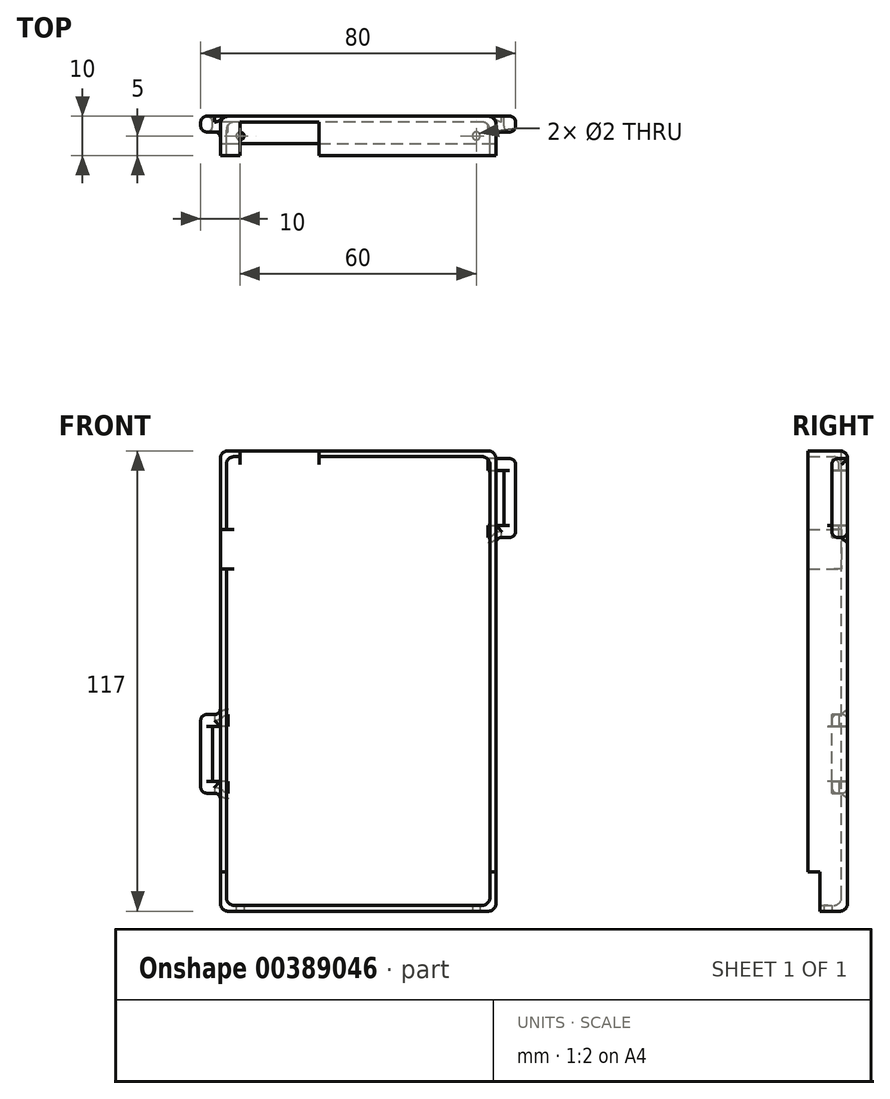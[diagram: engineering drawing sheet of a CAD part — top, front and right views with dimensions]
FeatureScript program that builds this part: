
annotation { "Feature Type Name" : "Feature", "Feature Type Description" : "" }
export const myFeature = defineFeature(function(context is Context, id is Id, definition is map)
    precondition{}
    {
        {
            var Q0;
            Q0=qCreatedBy(makeId("Front.planeOp"),FACE);
            var sketch = newSketch(context, id + "F0", { "sketchPlane" : qUnion([Q0])});
            skLineSegment(sketch, "E0.bottom", {"start": v(-70, 117) * mm, "end": v(0, 117) * mm});
            skLineSegment(sketch, "E0.top", {"start": v(-70, 0) * mm, "end": v(0, 0) * mm});
            skLineSegment(sketch, "E0.left", {"start": v(-70, 117) * mm, "end": v(-70, 0) * mm});
            skLineSegment(sketch, "E0.right", {"start": v(0, 117) * mm, "end": v(0, 0) * mm});
            skLineSegment(sketch, "E1.0", {"start": v(-68.5, 115.5) * mm, "end": v(-1.5, 115.5) * mm});
            skLineSegment(sketch, "E1.1", {"start": v(-68.5, 115.5) * mm, "end": v(-68.5, 1.5) * mm});
            skLineSegment(sketch, "E1.2", {"start": v(-68.5, 1.5) * mm, "end": v(-1.5, 1.5) * mm});
            skLineSegment(sketch, "E1.3", {"start": v(-1.5, 115.5) * mm, "end": v(-1.5, 1.5) * mm});
            skLineSegment(sketch, "E2.bottom", {"start": v(-70, 97) * mm, "end": v(-68.5, 97) * mm});
            skLineSegment(sketch, "E2.top", {"start": v(-70, 87) * mm, "end": v(-68.5, 87) * mm});
            skLineSegment(sketch, "E2.left", {"start": v(-70, 97) * mm, "end": v(-70, 87) * mm});
            skLineSegment(sketch, "E2.right", {"start": v(-68.5, 97) * mm, "end": v(-68.5, 87) * mm});
            skLineSegment(sketch, "E3.bottom", {"start": v(-65, 117) * mm, "end": v(-45, 117) * mm});
            skLineSegment(sketch, "E3.top", {"start": v(-65, 115.5) * mm, "end": v(-45, 115.5) * mm});
            skLineSegment(sketch, "E3.left", {"start": v(-65, 117) * mm, "end": v(-65, 115.5) * mm});
            skLineSegment(sketch, "E3.right", {"start": v(-45, 117) * mm, "end": v(-45, 115.5) * mm});
            skSolve(sketch);
        }
        {
            var Q0;
            Q0=qSketchRegion(id+"F0",true);
            var Q1;
            Q1=makeQuery(id+"F0.imprint","IMPRINT",FACE,{"disambiguationData":[TD([[makeQuery(id+"F0.imprint","IMPRINT",EDGE,{"derivedFrom":sQuery(id+"F0.wireOp",EDGE,"E0.bottom")}),-1.0]])]});
            var Q2;
            Q2=makeQuery(id+"F0.imprint","IMPRINT",FACE,{"disambiguationData":[TD([[makeQuery(id+"F0.imprint","IMPRINT",EDGE,{"derivedFrom":sQuery(id+"F0.wireOp",EDGE,"E1.0")}),-1.0]])]});
            extrude(context, id + "F1", {"entities" : qUnion([Q0, Q1, Q2]), "depth" : 1.5 * mm});
        }
        {
            var Q0;
            {var subQ4=sQuery(id+"F0.wireOp",EDGE,"E2.bottom");Q0=makeQuery(id+"F0.imprint","IMPRINT",FACE,{"disambiguationData":[TD([[makeQuery(id+"F0.imprint","IMPRINT",EDGE,{"derivedFrom":subQ4}),1.0]])]});}
            var Q1;
            {var subQ2=sQuery(id+"F0.wireOp",EDGE,"E0.top");Q1=makeQuery(id+"F0.imprint","IMPRINT",FACE,{"disambiguationData":[TD([[makeQuery(id+"F0.imprint","IMPRINT",EDGE,{"derivedFrom":subQ2}),1.0]])]});}
            extrude(context, id + "F2", {"entities" : qUnion([Q0, Q1]), "operationType" : NewBodyOperationType.ADD, "depth" : 10 * mm});
        }
        {
            var Q0;
            {var subQ0=sQuery(id+"F0.wireOp",EDGE,"E0.top");Q0=makeQuery(id+"F2.boolean.opBoolean","MERGE",FACE,{"derivedFrom":[makeQuery(id+"F1.opExtrude","SWEPT_FACE",FACE,{"disambiguationData":[OSD([subQ0])]}),makeQuery(id+"F2.opExtrude","SWEPT_FACE",FACE,{"disambiguationData":[OSD([subQ0])]})]});}
            var sketch = newSketch(context, id + "F3", { "sketchPlane" : qUnion([Q0])});
            skCircle(sketch, "E4", {"center": v(-65, 5) * mm, "radius": 1 * mm});
            skLineSegment(sketch, "E5.0", {"start": v(-70, 10) * mm, "end": v(0, 10) * mm});
            skLineSegment(sketch, "E6.0", {"start": v(-70, 10) * mm, "end": v(-70, 0) * mm});
            skCircle(sketch, "E7", {"center": v(-5, 5) * mm, "radius": 1 * mm});
            skSolve(sketch);
        }
        {
            var Q0;
            Q0=qSketchRegion(id+"F3",true);
            extrude(context, id + "F4", {"entities" : qUnion([Q0]), "operationType" : NewBodyOperationType.REMOVE, "oppositeDirection" : true, "depth" : 25 * mm});
        }
        {
            var Q0;
            Q0=makeQuery(id+"F1.opExtrude","CAP_EDGE",EDGE,{"disambiguationData":[OSD([sQuery(id+"F0.wireOp",EDGE,"E0.top")])],"isStart":true});
            var Q1;
            Q1=makeQuery(id+"F1.opExtrude","CAP_EDGE",EDGE,{"disambiguationData":[OSD([sQuery(id+"F0.wireOp",EDGE,"E0.right")])],"isStart":true});
            var Q2;
            Q2=makeQuery(id+"F1.opExtrude","CAP_EDGE",EDGE,{"disambiguationData":[OSD([sQuery(id+"F0.wireOp",EDGE,"E0.left"),sQuery(id+"F0.wireOp",EDGE,"E2.left")])],"isStart":true});
            var Q3;
            Q3=makeQuery(id+"F1.opExtrude","CAP_EDGE",EDGE,{"disambiguationData":[OSD([sQuery(id+"F0.wireOp",EDGE,"E0.bottom"),sQuery(id+"F0.wireOp",EDGE,"E3.bottom")])],"isStart":true});
            var Q4;
            Q4=makeQuery(id+"F2.boolean.opBoolean","INTERSECT",EDGE,{"derivedFrom":[makeQuery(id+"F1.opExtrude","CAP_FACE",FACE,{"disambiguationData":[OSD([sQuery(id+"F0.wireOp",EDGE,"E0.bottom"),sQuery(id+"F0.wireOp",EDGE,"E0.top"),sQuery(id+"F0.wireOp",EDGE,"E0.left"),sQuery(id+"F0.wireOp",EDGE,"E0.right"),sQuery(id+"F0.wireOp",EDGE,"E2.left"),sQuery(id+"F0.wireOp",EDGE,"E3.bottom")])],"isStart":false}),makeQuery(id+"F2.opExtrude","SWEPT_FACE",FACE,{"disambiguationData":[OSD([sQuery(id+"F0.wireOp",EDGE,"E1.2")])]})]});
            var Q5;
            {var subQ0=sQuery(id+"F0.wireOp",EDGE,"E1.1");Q5=makeQuery(id+"F2.boolean.opBoolean","INTERSECT",EDGE,{"derivedFrom":[makeQuery(id+"F1.opExtrude","CAP_FACE",FACE,{"disambiguationData":[OSD([sQuery(id+"F0.wireOp",EDGE,"E0.bottom"),sQuery(id+"F0.wireOp",EDGE,"E0.top"),sQuery(id+"F0.wireOp",EDGE,"E0.left"),sQuery(id+"F0.wireOp",EDGE,"E0.right"),sQuery(id+"F0.wireOp",EDGE,"E2.left"),sQuery(id+"F0.wireOp",EDGE,"E3.bottom")])],"isStart":false}),makeQuery(id+"F2.opExtrude","SWEPT_FACE",FACE,{"disambiguationData":[OSD([subQ0]),TDD([makeQuery(id+"F0.imprint","IMPRINT",EDGE,{"disambiguationData":[TD([[makeQuery(id+"F0.imprint","INTERSECT",VERTEX,{"derivedFrom":[subQ0,sQuery(id+"F0.wireOp",EDGE,"E1.2")]}),1.0]])],"derivedFrom":subQ0})])]})]});}
            var Q6;
            {var subQ0=sQuery(id+"F0.wireOp",EDGE,"E1.1");Q6=makeQuery(id+"F2.boolean.opBoolean","INTERSECT",EDGE,{"derivedFrom":[makeQuery(id+"F1.opExtrude","CAP_FACE",FACE,{"disambiguationData":[OSD([sQuery(id+"F0.wireOp",EDGE,"E0.bottom"),sQuery(id+"F0.wireOp",EDGE,"E0.top"),sQuery(id+"F0.wireOp",EDGE,"E0.left"),sQuery(id+"F0.wireOp",EDGE,"E0.right"),sQuery(id+"F0.wireOp",EDGE,"E2.left"),sQuery(id+"F0.wireOp",EDGE,"E3.bottom")])],"isStart":false}),makeQuery(id+"F2.opExtrude","SWEPT_FACE",FACE,{"disambiguationData":[OSD([subQ0]),TDD([makeQuery(id+"F0.imprint","IMPRINT",EDGE,{"disambiguationData":[TD([[makeQuery(id+"F0.imprint","INTERSECT",VERTEX,{"derivedFrom":[sQuery(id+"F0.wireOp",EDGE,"E1.0"),subQ0]}),-1.0]])],"derivedFrom":subQ0})])]})]});}
            var Q7;
            {var subQ0=sQuery(id+"F0.wireOp",EDGE,"E1.0");Q7=makeQuery(id+"F2.boolean.opBoolean","INTERSECT",EDGE,{"derivedFrom":[makeQuery(id+"F1.opExtrude","CAP_FACE",FACE,{"disambiguationData":[OSD([sQuery(id+"F0.wireOp",EDGE,"E0.bottom"),sQuery(id+"F0.wireOp",EDGE,"E0.top"),sQuery(id+"F0.wireOp",EDGE,"E0.left"),sQuery(id+"F0.wireOp",EDGE,"E0.right"),sQuery(id+"F0.wireOp",EDGE,"E2.left"),sQuery(id+"F0.wireOp",EDGE,"E3.bottom")])],"isStart":false}),makeQuery(id+"F2.opExtrude","SWEPT_FACE",FACE,{"disambiguationData":[OSD([subQ0]),TDD([makeQuery(id+"F0.imprint","IMPRINT",EDGE,{"disambiguationData":[TD([[makeQuery(id+"F0.imprint","INTERSECT",VERTEX,{"derivedFrom":[subQ0,sQuery(id+"F0.wireOp",EDGE,"E1.1")]}),-1.0]])],"derivedFrom":subQ0})])]})]});}
            var Q8;
            {var subQ0=sQuery(id+"F0.wireOp",EDGE,"E1.0");Q8=makeQuery(id+"F2.boolean.opBoolean","INTERSECT",EDGE,{"derivedFrom":[makeQuery(id+"F1.opExtrude","CAP_FACE",FACE,{"disambiguationData":[OSD([sQuery(id+"F0.wireOp",EDGE,"E0.bottom"),sQuery(id+"F0.wireOp",EDGE,"E0.top"),sQuery(id+"F0.wireOp",EDGE,"E0.left"),sQuery(id+"F0.wireOp",EDGE,"E0.right"),sQuery(id+"F0.wireOp",EDGE,"E2.left"),sQuery(id+"F0.wireOp",EDGE,"E3.bottom")])],"isStart":false}),makeQuery(id+"F2.opExtrude","SWEPT_FACE",FACE,{"disambiguationData":[OSD([subQ0]),TDD([makeQuery(id+"F0.imprint","IMPRINT",EDGE,{"disambiguationData":[TD([[makeQuery(id+"F0.imprint","INTERSECT",VERTEX,{"derivedFrom":[subQ0,sQuery(id+"F0.wireOp",EDGE,"E1.3")]}),1.0]])],"derivedFrom":subQ0})])]})]});}
            var Q9;
            Q9=makeQuery(id+"F2.boolean.opBoolean","INTERSECT",EDGE,{"derivedFrom":[makeQuery(id+"F1.opExtrude","CAP_FACE",FACE,{"disambiguationData":[OSD([sQuery(id+"F0.wireOp",EDGE,"E0.bottom"),sQuery(id+"F0.wireOp",EDGE,"E0.top"),sQuery(id+"F0.wireOp",EDGE,"E0.left"),sQuery(id+"F0.wireOp",EDGE,"E0.right"),sQuery(id+"F0.wireOp",EDGE,"E2.left"),sQuery(id+"F0.wireOp",EDGE,"E3.bottom")])],"isStart":false}),makeQuery(id+"F2.opExtrude","SWEPT_FACE",FACE,{"disambiguationData":[OSD([sQuery(id+"F0.wireOp",EDGE,"E1.3")])]})]});
            fillet(context, id + "F5", {"entities" : qUnion([Q0, Q1, Q2, Q3, Q4, Q5, Q6, Q7, Q8, Q9]), "radius" : 2 * mm, "tangentPropagation" : true, "allowEdgeOverflow" : false});
        }
        {
            var Q0;
            {var subQ0=sQuery(id+"F0.wireOp",EDGE,"E0.left");var subQ1=sQuery(id+"F0.wireOp",EDGE,"E0.top");Q0=makeQuery(id+"F2.boolean.opBoolean","MERGE",EDGE,{"derivedFrom":[makeQuery(id+"F1.opExtrude","SWEPT_EDGE",EDGE,{"disambiguationData":[OSD([subQ1,subQ0])]}),makeQuery(id+"F2.opExtrude","SWEPT_EDGE",EDGE,{"disambiguationData":[OSD([subQ1,subQ0])]})]});}
            var Q1;
            {var subQ0=sQuery(id+"F0.wireOp",EDGE,"E0.right");var subQ1=sQuery(id+"F0.wireOp",EDGE,"E0.top");Q1=makeQuery(id+"F2.boolean.opBoolean","MERGE",EDGE,{"derivedFrom":[makeQuery(id+"F1.opExtrude","SWEPT_EDGE",EDGE,{"disambiguationData":[OSD([subQ1,subQ0])]}),makeQuery(id+"F2.opExtrude","SWEPT_EDGE",EDGE,{"disambiguationData":[OSD([subQ1,subQ0])]})]});}
            var Q2;
            Q2=makeQuery(id+"F2.opExtrude","SWEPT_EDGE",EDGE,{"disambiguationData":[OSD([sQuery(id+"F0.wireOp",EDGE,"E1.1"),sQuery(id+"F0.wireOp",EDGE,"E1.2")])]});
            var Q3;
            Q3=makeQuery(id+"F2.opExtrude","SWEPT_EDGE",EDGE,{"disambiguationData":[OSD([sQuery(id+"F0.wireOp",EDGE,"E1.2"),sQuery(id+"F0.wireOp",EDGE,"E1.3")])]});
            var Q4;
            {var subQ0=sQuery(id+"F0.wireOp",EDGE,"E0.left");var subQ1=sQuery(id+"F0.wireOp",EDGE,"E0.bottom");Q4=makeQuery(id+"F2.boolean.opBoolean","MERGE",EDGE,{"derivedFrom":[makeQuery(id+"F1.opExtrude","SWEPT_EDGE",EDGE,{"disambiguationData":[OSD([subQ1,subQ0])]}),makeQuery(id+"F2.opExtrude","SWEPT_EDGE",EDGE,{"disambiguationData":[OSD([subQ1,subQ0])]})]});}
            var Q5;
            Q5=makeQuery(id+"F2.opExtrude","SWEPT_EDGE",EDGE,{"disambiguationData":[OSD([sQuery(id+"F0.wireOp",EDGE,"E1.0"),sQuery(id+"F0.wireOp",EDGE,"E1.1")])]});
            var Q6;
            {var subQ0=sQuery(id+"F0.wireOp",EDGE,"E1.1");var subQ1=sQuery(id+"F0.wireOp",EDGE,"E1.0");var subQ2=makeQuery(id+"F0.imprint","INTERSECT",VERTEX,{"derivedFrom":[subQ1,subQ0]});var subQ3=makeQuery(id+"F1.opExtrude","CAP_FACE",FACE,{"disambiguationData":[OSD([sQuery(id+"F0.wireOp",EDGE,"E0.bottom"),sQuery(id+"F0.wireOp",EDGE,"E0.top"),sQuery(id+"F0.wireOp",EDGE,"E0.left"),sQuery(id+"F0.wireOp",EDGE,"E0.right"),sQuery(id+"F0.wireOp",EDGE,"E2.left"),sQuery(id+"F0.wireOp",EDGE,"E3.bottom")])],"isStart":false});Q6=makeQuery(id+"F5.opFillet","BLEND_EDGE",EDGE,{"blendedFrom":[makeQuery(id+"F2.boolean.opBoolean","INTERSECT",EDGE,{"derivedFrom":[subQ3,makeQuery(id+"F2.opExtrude","SWEPT_FACE",FACE,{"disambiguationData":[OSD([subQ1]),TDD([makeQuery(id+"F0.imprint","IMPRINT",EDGE,{"disambiguationData":[TD([[subQ2,-1.0]])],"derivedFrom":subQ1})])]})]}),makeQuery(id+"F2.boolean.opBoolean","INTERSECT",EDGE,{"derivedFrom":[subQ3,makeQuery(id+"F2.opExtrude","SWEPT_FACE",FACE,{"disambiguationData":[OSD([subQ0]),TDD([makeQuery(id+"F0.imprint","IMPRINT",EDGE,{"disambiguationData":[TD([[subQ2,-1.0]])],"derivedFrom":subQ0})])]})]})],"blendedInto":[]});}
            var Q7;
            {var subQ0=sQuery(id+"F0.wireOp",EDGE,"E0.right");var subQ1=sQuery(id+"F0.wireOp",EDGE,"E0.bottom");Q7=makeQuery(id+"F2.boolean.opBoolean","MERGE",EDGE,{"derivedFrom":[makeQuery(id+"F1.opExtrude","SWEPT_EDGE",EDGE,{"disambiguationData":[OSD([subQ1,subQ0])]}),makeQuery(id+"F2.opExtrude","SWEPT_EDGE",EDGE,{"disambiguationData":[OSD([subQ1,subQ0])]})]});}
            var Q8;
            Q8=makeQuery(id+"F2.opExtrude","SWEPT_EDGE",EDGE,{"disambiguationData":[OSD([sQuery(id+"F0.wireOp",EDGE,"E1.0"),sQuery(id+"F0.wireOp",EDGE,"E1.3")])]});
            fillet(context, id + "F6", {"entities" : qUnion([Q0, Q1, Q2, Q3, Q4, Q5, Q6, Q7, Q8]), "radius" : 2 * mm, "tangentPropagation" : true, "allowEdgeOverflow" : false});
        }
        {
            var Q0;
            Q0=makeQuery(id+"F2.opExtrude","CAP_FACE",FACE,{"disambiguationData":[OSD([sQuery(id+"F0.wireOp",EDGE,"E0.bottom"),sQuery(id+"F0.wireOp",EDGE,"E0.top"),sQuery(id+"F0.wireOp",EDGE,"E0.left"),sQuery(id+"F0.wireOp",EDGE,"E0.right"),sQuery(id+"F0.wireOp",EDGE,"E1.0"),sQuery(id+"F0.wireOp",EDGE,"E1.1"),sQuery(id+"F0.wireOp",EDGE,"E1.2"),sQuery(id+"F0.wireOp",EDGE,"E1.3"),sQuery(id+"F0.wireOp",EDGE,"E2.top"),sQuery(id+"F0.wireOp",EDGE,"E3.right")])],"isStart":false});
            var sketch = newSketch(context, id + "F7", { "sketchPlane" : qUnion([Q0])});
            skLineSegment(sketch, "E8.bottom", {"start": v(-70, 2) * mm, "end": v(0, 2) * mm});
            skLineSegment(sketch, "E8.top", {"start": v(-70, 0) * mm, "end": v(0, 0) * mm});
            skLineSegment(sketch, "E8.left", {"start": v(-70, 2) * mm, "end": v(-70, 0) * mm});
            skLineSegment(sketch, "E8.right", {"start": v(0, 2) * mm, "end": v(0, 0) * mm});
            skLineSegment(sketch, "E9.top", {"start": v(-70, 10) * mm, "end": v(0, 10) * mm});
            skLineSegment(sketch, "E9.left", {"start": v(-70, 2) * mm, "end": v(-70, 10) * mm});
            skLineSegment(sketch, "E9.right", {"start": v(0, 2) * mm, "end": v(0, 10) * mm});
            skSolve(sketch);
        }
        {
            var Q0;
            {var subQ10=sQuery(id+"F7.wireOp",EDGE,"E9.right");Q0=makeQuery(id+"F7.imprint","IMPRINT",FACE,{"disambiguationData":[TD([[makeQuery(id+"F7.imprint","IMPRINT",EDGE,{"derivedFrom":subQ10}),-1.0]])]});}
            var Q1;
            {var subQ0=sQuery(id+"F0.wireOp",EDGE,"E1.2");var subQ1=makeQuery(id+"F2.opExtrude","CAP_EDGE",EDGE,{"disambiguationData":[OSD([subQ0])],"isStart":false});Q1=makeQuery(id+"F7.imprint","IMPRINT",FACE,{"disambiguationData":[TD([[makeQuery(id+"F7.imprint","IMPRINT",EDGE,{"derivedFrom":subQ1}),-1.0]])]});}
            var Q2;
            {var subQ1=sQuery(id+"F0.wireOp",EDGE,"E1.3");var subQ6=makeQuery(id+"F2.opExtrude","CAP_EDGE",EDGE,{"disambiguationData":[OSD([subQ1])],"isStart":false});var subQ8=sQuery(id+"F7.wireOp",EDGE,"E9.top");var subQ9=makeQuery(id+"F7.imprint","INTERSECT",VERTEX,{"derivedFrom":[subQ6,subQ8]});Q2=makeQuery(id+"F7.imprint","IMPRINT",FACE,{"disambiguationData":[TD([[makeQuery(id+"F7.imprint","IMPRINT",EDGE,{"disambiguationData":[TD([[subQ9,1.0]])],"derivedFrom":subQ8}),-1.0]])]});}
            var Q3;
            {var subQ11=sQuery(id+"F7.wireOp",EDGE,"E9.left");Q3=makeQuery(id+"F7.imprint","IMPRINT",FACE,{"disambiguationData":[TD([[makeQuery(id+"F7.imprint","IMPRINT",EDGE,{"derivedFrom":subQ11}),1.0]])]});}
            extrude(context, id + "F8", {"entities" : qUnion([Q0, Q1, Q2, Q3]), "operationType" : NewBodyOperationType.REMOVE, "oppositeDirection" : true, "depth" : 3 * mm});
        }
        {
            var Q0;
            Q0=makeQuery(id+"F1.opExtrude","CAP_FACE",FACE,{"disambiguationData":[OSD([sQuery(id+"F0.wireOp",EDGE,"E0.bottom"),sQuery(id+"F0.wireOp",EDGE,"E0.top"),sQuery(id+"F0.wireOp",EDGE,"E0.left"),sQuery(id+"F0.wireOp",EDGE,"E0.right"),sQuery(id+"F0.wireOp",EDGE,"E2.left"),sQuery(id+"F0.wireOp",EDGE,"E3.bottom")])],"isStart":true});
            var sketch = newSketch(context, id + "F9", { "sketchPlane" : qUnion([Q0])});
            skLineSegment(sketch, "E10.bottom", {"start": v(-5, 115) * mm, "end": v(-2, 115) * mm});
            skLineSegment(sketch, "E10.top", {"start": v(-5, 95) * mm, "end": v(-2, 95) * mm});
            skLineSegment(sketch, "E10.left", {"start": v(-5, 115) * mm, "end": v(-5, 95) * mm});
            skLineSegment(sketch, "E10.right", {"start": v(-2, 115) * mm, "end": v(-2, 95) * mm});
            skLineSegment(sketch, "E11.bottom", {"start": v(-2, 95) * mm, "end": v(2, 95) * mm});
            skLineSegment(sketch, "E11.top", {"start": v(-2, 98) * mm, "end": v(2, 98) * mm});
            skLineSegment(sketch, "E11.left", {"start": v(-2, 95) * mm, "end": v(-2, 98) * mm});
            skLineSegment(sketch, "E11.right", {"start": v(2, 95) * mm, "end": v(2, 98) * mm});
            skLineSegment(sketch, "E12.bottom", {"start": v(-2, 115) * mm, "end": v(2, 115) * mm});
            skLineSegment(sketch, "E12.top", {"start": v(-2, 112) * mm, "end": v(2, 112) * mm});
            skLineSegment(sketch, "E12.left", {"start": v(-2, 115) * mm, "end": v(-2, 112) * mm});
            skLineSegment(sketch, "E12.right", {"start": v(2, 115) * mm, "end": v(2, 112) * mm});
            skPoint(sketch, "E13.0", {"position": v(2, 95) * mm});
            skPoint(sketch, "E14.0", {"position": v(70, 2) * mm});
            skLineSegment(sketch, "E15.0", {"start": v(68, 0) * mm, "end": v(2, 0) * mm});
            skPoint(sketch, "E16.0", {"position": v(2, 2) * mm});
            skLineSegment(sketch, "E17.bottom", {"start": v(75, 50) * mm, "end": v(72, 50) * mm});
            skLineSegment(sketch, "E17.top", {"start": v(75, 30) * mm, "end": v(72, 30) * mm});
            skLineSegment(sketch, "E17.left", {"start": v(75, 50) * mm, "end": v(75, 30) * mm});
            skLineSegment(sketch, "E17.right", {"start": v(72, 50) * mm, "end": v(72, 30) * mm});
            skLineSegment(sketch, "E18.bottom", {"start": v(72, 50) * mm, "end": v(68, 50) * mm});
            skLineSegment(sketch, "E18.top", {"start": v(72, 47) * mm, "end": v(68, 47) * mm});
            skLineSegment(sketch, "E18.left", {"start": v(72, 50) * mm, "end": v(72, 47) * mm});
            skLineSegment(sketch, "E18.right", {"start": v(68, 50) * mm, "end": v(68, 47) * mm});
            skLineSegment(sketch, "E19.bottom", {"start": v(72, 30) * mm, "end": v(68, 30) * mm});
            skLineSegment(sketch, "E19.top", {"start": v(72, 33) * mm, "end": v(68, 33) * mm});
            skLineSegment(sketch, "E19.left", {"start": v(72, 30) * mm, "end": v(72, 33) * mm});
            skLineSegment(sketch, "E19.right", {"start": v(68, 30) * mm, "end": v(68, 33) * mm});
            skPoint(sketch, "E20.0", {"position": v(68, 2) * mm});
            skLineSegment(sketch, "E21.0", {"start": v(68, 2) * mm, "end": v(68, 115) * mm});
            skPoint(sketch, "E22.0", {"position": v(2, 115) * mm});
            skSolve(sketch);
        }
        {
            var Q0;
            Q0=makeQuery(id+"F9.imprint","IMPRINT",FACE,{"disambiguationData":[TD([[makeQuery(id+"F9.imprint","IMPRINT",EDGE,{"derivedFrom":sQuery(id+"F9.wireOp",EDGE,"E10.bottom")}),-1.0]])]});
            var Q1;
            Q1=makeQuery(id+"F9.imprint","IMPRINT",FACE,{"disambiguationData":[TD([[makeQuery(id+"F9.imprint","IMPRINT",EDGE,{"derivedFrom":sQuery(id+"F9.wireOp",EDGE,"E11.bottom")}),1.0]])]});
            var Q2;
            Q2=makeQuery(id+"F9.imprint","IMPRINT",FACE,{"disambiguationData":[TD([[makeQuery(id+"F9.imprint","IMPRINT",EDGE,{"derivedFrom":sQuery(id+"F9.wireOp",EDGE,"E12.bottom")}),-1.0]])]});
            var Q3;
            Q3=makeQuery(id+"F9.imprint","IMPRINT",FACE,{"disambiguationData":[TD([[makeQuery(id+"F9.imprint","IMPRINT",EDGE,{"derivedFrom":sQuery(id+"F9.wireOp",EDGE,"E17.bottom")}),1.0]])]});
            var Q4;
            {var subQ0=sQuery(id+"F9.wireOp",EDGE,"E18.bottom");Q4=makeQuery(id+"F9.imprint","IMPRINT",FACE,{"disambiguationData":[TD([[makeQuery(id+"F9.imprint","IMPRINT",EDGE,{"derivedFrom":subQ0}),1.0]])]});}
            var Q5;
            {var subQ0=sQuery(id+"F9.wireOp",EDGE,"E19.bottom");Q5=makeQuery(id+"F9.imprint","IMPRINT",FACE,{"disambiguationData":[TD([[makeQuery(id+"F9.imprint","IMPRINT",EDGE,{"derivedFrom":subQ0}),-1.0]])]});}
            extrude(context, id + "F10", {"entities" : qUnion([Q0, Q1, Q2, Q3, Q4, Q5]), "operationType" : NewBodyOperationType.ADD, "oppositeDirection" : true, "depth" : 4 * mm});
        }
        {
            var Q0;
            Q0=makeQuery(id+"F10.opExtrude","SWEPT_FACE",FACE,{"disambiguationData":[OSD([sQuery(id+"F9.wireOp",EDGE,"E10.left")])]});
            var Q1;
            Q1=makeQuery(id+"F10.opExtrude","SWEPT_FACE",FACE,{"disambiguationData":[OSD([sQuery(id+"F9.wireOp",EDGE,"E17.left")])]});
            var Q2;
            {var subQ6=sQuery(id+"F9.wireOp",EDGE,"E19.bottom");var subQ10=sQuery(id+"F9.wireOp",EDGE,"E17.left");var subQ11=sQuery(id+"F9.wireOp",EDGE,"E17.top");Q2=makeQuery(id+"F10.boolean.opBoolean","SPLIT",FACE,{"disambiguationData":[TD([makeQuery(id+"F10.opExtrude","SWEPT_FACE",FACE,{"disambiguationData":[OSD([subQ10])]})])],"derivedFrom":makeQuery(id+"F10.opExtrude","SWEPT_FACE",FACE,{"disambiguationData":[OSD([subQ11,subQ6])]})});}
            var Q3;
            {var subQ8=sQuery(id+"F9.wireOp",EDGE,"E18.bottom");var subQ10=sQuery(id+"F9.wireOp",EDGE,"E17.left");var subQ12=sQuery(id+"F9.wireOp",EDGE,"E17.bottom");Q3=makeQuery(id+"F10.boolean.opBoolean","SPLIT",FACE,{"disambiguationData":[TD([makeQuery(id+"F10.opExtrude","SWEPT_FACE",FACE,{"disambiguationData":[OSD([subQ10])]})])],"derivedFrom":makeQuery(id+"F10.opExtrude","SWEPT_FACE",FACE,{"disambiguationData":[OSD([subQ12,subQ8])]})});}
            var Q4;
            Q4=makeQuery(id+"F10.opExtrude","CAP_EDGE",EDGE,{"disambiguationData":[OSD([sQuery(id+"F9.wireOp",EDGE,"E17.right")])],"isStart":false});
            var Q5;
            Q5=makeQuery(id+"F10.opExtrude","CAP_EDGE",EDGE,{"disambiguationData":[OSD([sQuery(id+"F9.wireOp",EDGE,"E17.right")])],"isStart":true});
            var Q6;
            Q6=makeQuery(id+"F10.opExtrude","CAP_EDGE",EDGE,{"disambiguationData":[OSD([sQuery(id+"F9.wireOp",EDGE,"E10.right")])],"isStart":false});
            var Q7;
            {var subQ0=sQuery(id+"F0.wireOp",EDGE,"E0.right");var subQ6=sQuery(id+"F9.wireOp",EDGE,"E11.bottom");var subQ9=sQuery(id+"F9.wireOp",EDGE,"E10.top");Q7=makeQuery(id+"F10.boolean.opBoolean","SPLIT",FACE,{"disambiguationData":[TD([makeQuery(id+"F1.opExtrude","SWEPT_FACE",FACE,{"disambiguationData":[OSD([subQ0])]})])],"derivedFrom":makeQuery(id+"F10.opExtrude","SWEPT_FACE",FACE,{"disambiguationData":[OSD([subQ9,subQ6])]})});}
            var Q8;
            Q8=makeQuery(id+"F10.opExtrude","CAP_EDGE",EDGE,{"disambiguationData":[OSD([sQuery(id+"F9.wireOp",EDGE,"E10.bottom"),sQuery(id+"F9.wireOp",EDGE,"E12.bottom")])],"isStart":false});
            fillet(context, id + "F11", {"entities" : qUnion([Q0, Q1, Q2, Q3, Q4, Q5, Q6, Q7, Q8]), "radius" : 1.5 * mm, "tangentPropagation" : true, "allowEdgeOverflow" : false});
        }
    });
